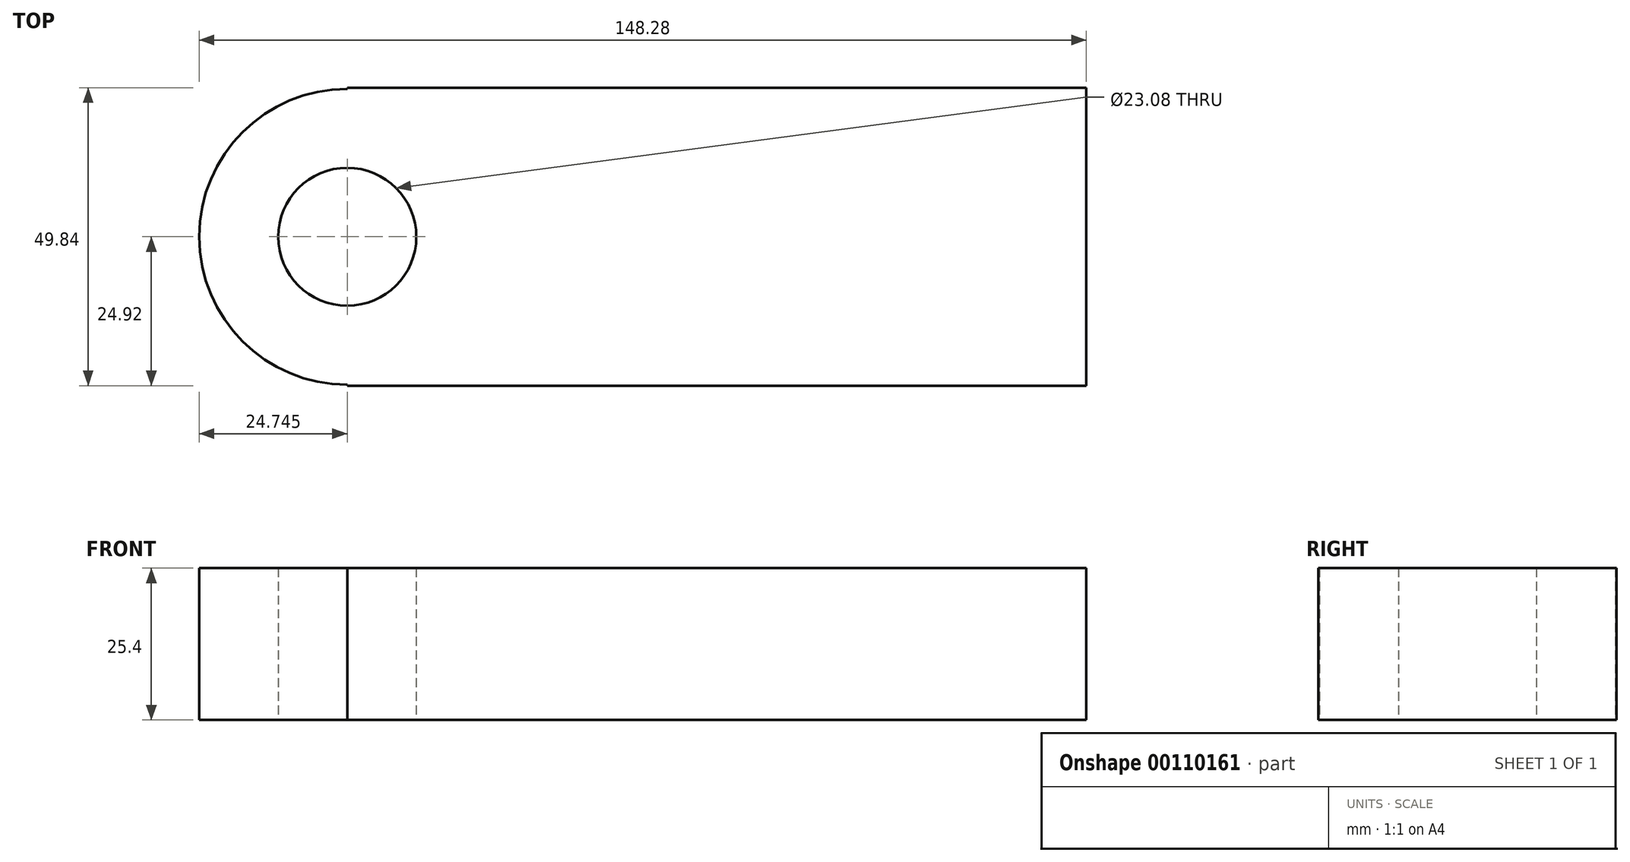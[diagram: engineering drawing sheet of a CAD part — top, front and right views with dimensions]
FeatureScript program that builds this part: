
annotation { "Feature Type Name" : "Feature", "Feature Type Description" : "" }
export const myFeature = defineFeature(function(context is Context, id is Id, definition is map)
    precondition{}
    {
        {
            var Q0;
            Q0=qCreatedBy(makeId("Top.planeOp"),FACE);
            var sketch = newSketch(context, id + "F0", { "sketchPlane" : qUnion([Q0])});
            skLineSegment(sketch, "E0.bottom", {"start": v(-61.77, -24.92) * mm, "end": v(61.77, -24.92) * mm});
            skLineSegment(sketch, "E0.top", {"start": v(-61.77, 24.92) * mm, "end": v(61.77, 24.92) * mm});
            skLineSegment(sketch, "E0.left", {"start": v(-61.77, -24.92) * mm, "end": v(-61.77, 24.92) * mm});
            skLineSegment(sketch, "E0.right", {"start": v(61.77, -24.92) * mm, "end": v(61.77, 24.92) * mm});
            skPoint(sketch, "E0.middle", {"position": v(0, 0) * mm});
            skCircle(sketch, "E1", {"center": v(-61.77, 0) * mm, "radius": 24.75 * mm});
            skCircle(sketch, "E2", {"center": v(-61.77, 0) * mm, "radius": 11.54 * mm});
            skSolve(sketch);
        }
        {
            var Q0;
            Q0 = qSketchRegion(id + "F0", true);
            extrude(context, id + "F1", {"entities" : qUnion([Q0]), "depth" : 25.4 * mm});
        }
    });
